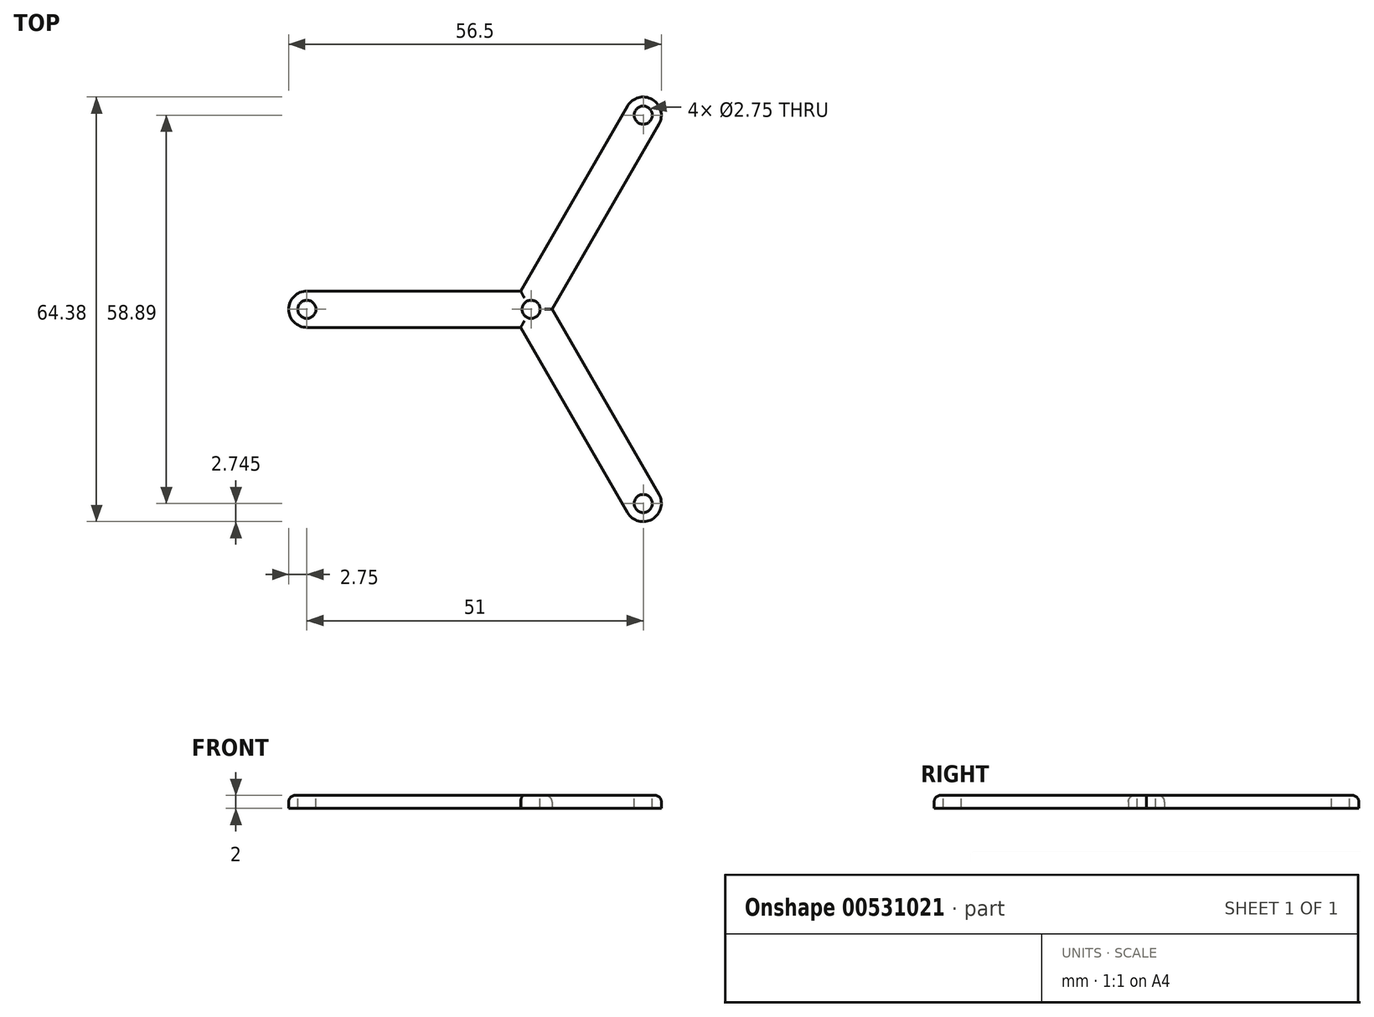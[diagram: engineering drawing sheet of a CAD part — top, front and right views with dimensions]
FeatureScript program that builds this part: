
annotation { "Feature Type Name" : "Feature", "Feature Type Description" : "" }
export const myFeature = defineFeature(function(context is Context, id is Id, definition is map)
    precondition{}
    {
        {
            var Q0;
            Q0=qCreatedBy(makeId("Top.planeOp"),FACE);
            var sketch = newSketch(context, id + "F0", { "sketchPlane" : qUnion([Q0])});
            skCircle(sketch, "E0", {"center": v(0, 0) * mm, "radius": 2.75 * mm, "construction": true});
            skLineSegment(sketch, "E1", {"start": v(0, 0) * mm, "end": v(-34, 0) * mm, "construction": true});
            skCircle(sketch, "E2", {"center": v(-34, 0) * mm, "radius": 2.75 * mm});
            skLineSegment(sketch, "E3", {"start": v(-34, 2.75) * mm, "end": v(0, 2.75) * mm});
            skLineSegment(sketch, "E4", {"start": v(-34, -2.75) * mm, "end": v(0, -2.75) * mm});
            skCircle(sketch, "E5.1.0", {"center": v(17, -29.44) * mm, "radius": 2.75 * mm});
            skLineSegment(sketch, "E5.1.1", {"start": v(14.62, -30.82) * mm, "end": v(-2.38, -1.37) * mm});
            skLineSegment(sketch, "E5.1.2", {"start": v(19.38, -28.07) * mm, "end": v(2.38, 1.38) * mm});
            skCircle(sketch, "E5.2.0", {"center": v(17, 29.44) * mm, "radius": 2.75 * mm});
            skLineSegment(sketch, "E5.2.1", {"start": v(19.38, 28.07) * mm, "end": v(2.38, -1.38) * mm});
            skLineSegment(sketch, "E5.2.2", {"start": v(14.62, 30.82) * mm, "end": v(-2.38, 1.38) * mm});
            skSolve(sketch);
        }
        {
            var Q0;
            Q0 = qSketchRegion(id + "F0", true);
            extrude(context, id + "F1", {"entities" : qUnion([Q0]), "depth" : 2 * mm, "offsetDistance" : 25 * mm});
        }
        {
            var Q0;
            Q0=makeQuery(id+"F1.opExtrude","CAP_FACE",FACE,{"disambiguationData":[OSD([sQuery(id+"F0.wireOp",EDGE,"E2"),sQuery(id+"F0.wireOp",EDGE,"E3"),sQuery(id+"F0.wireOp",EDGE,"E4"),sQuery(id+"F0.wireOp",EDGE,"E5.1.0"),sQuery(id+"F0.wireOp",EDGE,"E5.1.1"),sQuery(id+"F0.wireOp",EDGE,"E5.1.2"),sQuery(id+"F0.wireOp",EDGE,"E5.2.0"),sQuery(id+"F0.wireOp",EDGE,"E5.2.1"),sQuery(id+"F0.wireOp",EDGE,"E5.2.2")])],"isStart":false});
            var sketch = newSketch(context, id + "F2", { "sketchPlane" : qUnion([Q0])});
            skLineSegment(sketch, "E6", {"start": v(0, 0) * mm, "end": v(-34, 0) * mm, "construction": true});
            skCircle(sketch, "E7", {"center": v(-34, 0) * mm, "radius": 1.38 * mm});
            skCircle(sketch, "E8.1.0", {"center": v(17, -29.44) * mm, "radius": 1.38 * mm});
            skCircle(sketch, "E8.2.0", {"center": v(17, 29.44) * mm, "radius": 1.38 * mm});
            skPoint(sketch, "E8.center", {"position": v(0, 0) * mm});
            skCircle(sketch, "E9", {"center": v(0, 0) * mm, "radius": 1.38 * mm});
            skSolve(sketch);
        }
        {
            var Q0;
            Q0=makeQuery(id+"F2.imprint","IMPRINT",FACE,{"disambiguationData":[TD([[makeQuery(id+"F2.imprint","IMPRINT",EDGE,{"derivedFrom":sQuery(id+"F2.wireOp",EDGE,"E7")}),1.0]])]});
            var Q1;
            Q1=makeQuery(id+"F2.imprint","IMPRINT",FACE,{"disambiguationData":[TD([[makeQuery(id+"F2.imprint","IMPRINT",EDGE,{"derivedFrom":sQuery(id+"F2.wireOp",EDGE,"E8.2.0")}),1.0]])]});
            var Q2;
            Q2=makeQuery(id+"F2.imprint","IMPRINT",FACE,{"disambiguationData":[TD([[makeQuery(id+"F2.imprint","IMPRINT",EDGE,{"derivedFrom":sQuery(id+"F2.wireOp",EDGE,"E9")}),1.0]])]});
            var Q3;
            Q3=makeQuery(id+"F2.imprint","IMPRINT",FACE,{"disambiguationData":[TD([[makeQuery(id+"F2.imprint","IMPRINT",EDGE,{"derivedFrom":sQuery(id+"F2.wireOp",EDGE,"E8.1.0")}),1.0]])]});
            var Q4;
            Q4=makeQuery(id+"F1.opExtrude","CAP_FACE",FACE,{"disambiguationData":[OSD([sQuery(id+"F0.wireOp",EDGE,"E2"),sQuery(id+"F0.wireOp",EDGE,"E3"),sQuery(id+"F0.wireOp",EDGE,"E4"),sQuery(id+"F0.wireOp",EDGE,"E5.1.0"),sQuery(id+"F0.wireOp",EDGE,"E5.1.1"),sQuery(id+"F0.wireOp",EDGE,"E5.1.2"),sQuery(id+"F0.wireOp",EDGE,"E5.2.0"),sQuery(id+"F0.wireOp",EDGE,"E5.2.1"),sQuery(id+"F0.wireOp",EDGE,"E5.2.2")])],"isStart":true});
            extrude(context, id + "F3", {"entities" : qUnion([Q0, Q1, Q2, Q3]), "operationType" : NewBodyOperationType.REMOVE, "endBound" : BoundingType.UP_TO_SURFACE, "oppositeDirection" : true, "depth" : 25 * mm, "endBoundEntityFace" : qUnion([Q4]), "offsetDistance" : 25 * mm});
        }
        {
            var Q0;
            Q0=makeQuery(id+"F1.opExtrude","CAP_EDGE",EDGE,{"disambiguationData":[OSD([sQuery(id+"F0.wireOp",EDGE,"E5.2.0")])],"isStart":false});
            var Q1;
            Q1=makeQuery(id+"F1.opExtrude","CAP_EDGE",EDGE,{"disambiguationData":[OSD([sQuery(id+"F0.wireOp",EDGE,"E5.2.1")])],"isStart":false});
            var Q2;
            Q2=makeQuery(id+"F1.opExtrude","CAP_EDGE",EDGE,{"disambiguationData":[OSD([sQuery(id+"F0.wireOp",EDGE,"E3")])],"isStart":false});
            var Q3;
            Q3=makeQuery(id+"F1.opExtrude","CAP_EDGE",EDGE,{"disambiguationData":[OSD([sQuery(id+"F0.wireOp",EDGE,"E5.1.1")])],"isStart":false});
            fillet(context, id + "F4", {"entities" : qUnion([Q0, Q1, Q2, Q3]), "radius" : 1 * mm, "tangentPropagation" : true, "allowEdgeOverflow" : false});
        }
    });
